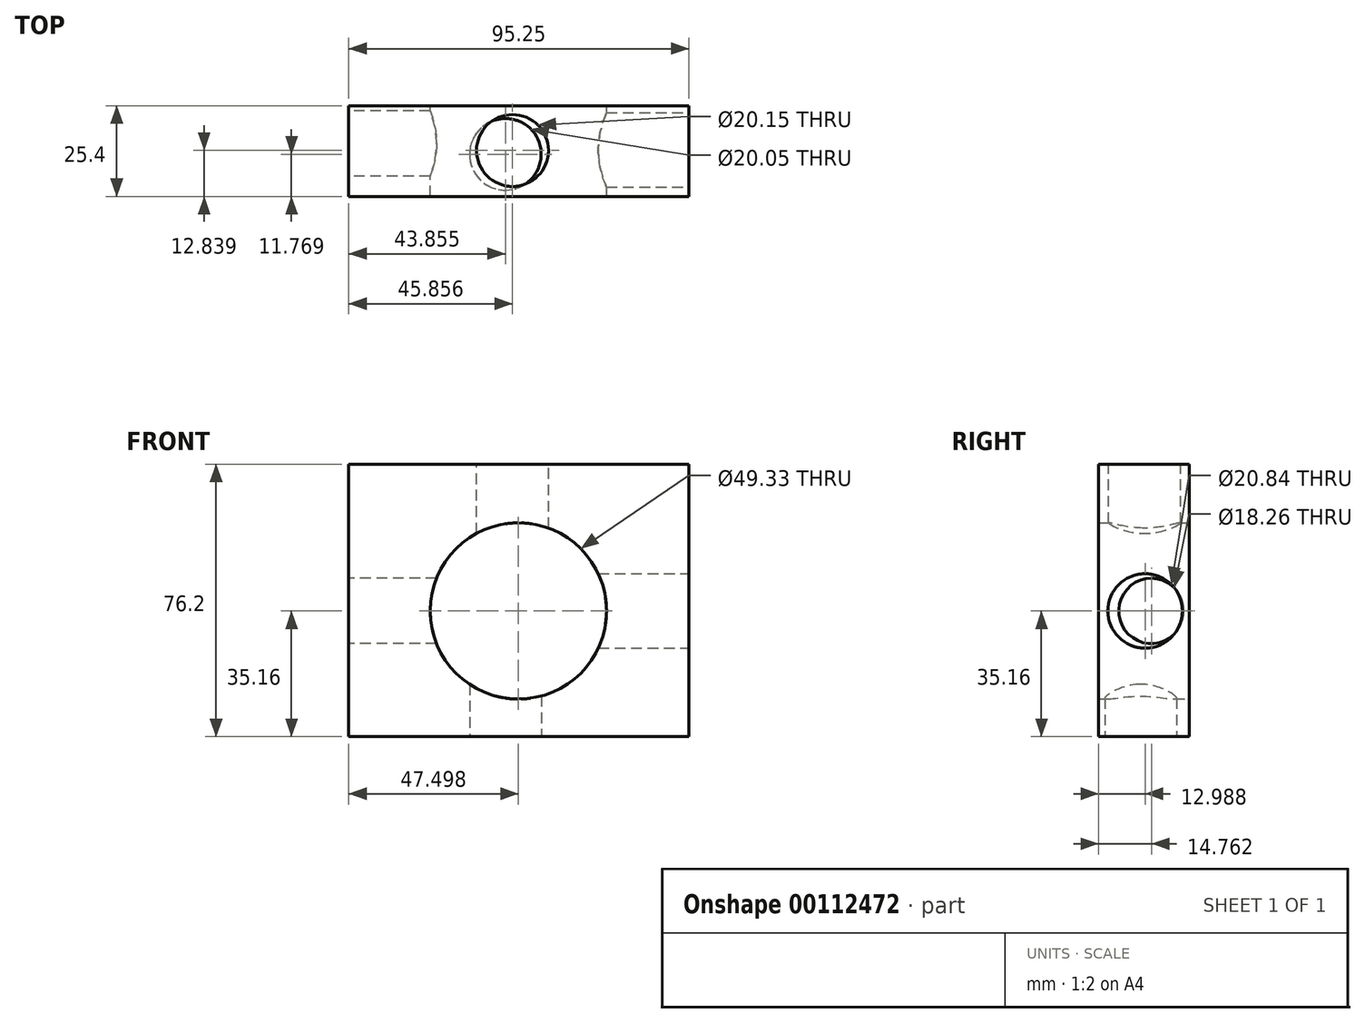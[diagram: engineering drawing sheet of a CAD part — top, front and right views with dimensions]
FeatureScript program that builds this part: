
annotation { "Feature Type Name" : "Feature", "Feature Type Description" : "" }
export const myFeature = defineFeature(function(context is Context, id is Id, definition is map)
    precondition{}
    {
        {
            var Q0;
            Q0=qCreatedBy(makeId("Front.planeOp"),FACE);
            var sketch = newSketch(context, id + "F0", { "sketchPlane" : qUnion([Q0])});
            skLineSegment(sketch, "E0", {"start": v(-95.25, 41.04) * mm, "end": v(0, 41.04) * mm});
            skLineSegment(sketch, "E1", {"start": v(0, 41.04) * mm, "end": v(0, -35.16) * mm});
            skLineSegment(sketch, "E2", {"start": v(0, -35.16) * mm, "end": v(-95.25, -35.16) * mm});
            skLineSegment(sketch, "E3", {"start": v(-95.25, -35.16) * mm, "end": v(-95.25, 41.04) * mm});
            skCircle(sketch, "E4", {"center": v(-47.75, 0) * mm, "radius": 24.67 * mm});
            skSolve(sketch);
        }
        {
            var Q0;
            Q0=makeQuery(id+"F0.imprint","IMPRINT",FACE,{"disambiguationData":[TD([[makeQuery(id+"F0.imprint","IMPRINT",EDGE,{"derivedFrom":sQuery(id+"F0.wireOp",EDGE,"E0")}),-1.0]])]});
            extrude(context, id + "F1", {"entities" : qUnion([Q0]), "depth" : 25.4 * mm});
        }
        {
            var Q0;
            Q0=makeQuery(id+"F1.opExtrude","SWEPT_FACE",FACE,{"disambiguationData":[OSD([sQuery(id+"F0.wireOp",EDGE,"E0")])]});
            var sketch = newSketch(context, id + "F2", { "sketchPlane" : qUnion([Q0])});
            skSolve(sketch);
        }
        {
            var Q0;
            {var subQ0=sQuery(id+"F0.wireOp",EDGE,"E0");Q0=makeQuery(id+"F2.imprint","IMPRINT",FACE,{"disambiguationData":[TD([[makeQuery(id+"F2.imprint","IMPRINT",EDGE,{"derivedFrom":makeQuery(id+"F1.opExtrude","CAP_EDGE",EDGE,{"disambiguationData":[OSD([subQ0])],"isStart":true})}),-1.0]])]});}
            var sketch = newSketch(context, id + "F3", { "sketchPlane" : qUnion([Q0])});
            skCircle(sketch, "E5", {"center": v(-49.4, -12.56) * mm, "radius": 10.07 * mm});
            skSolve(sketch);
        }
        {
            var Q0;
            Q0 = qSketchRegion(id + "F3", true);
            extrude(context, id + "F4", {"entities" : qUnion([Q0]), "operationType" : NewBodyOperationType.REMOVE, "oppositeDirection" : true, "depth" : 25.4 * mm});
        }
        {
            var Q0;
            Q0=makeQuery(id+"F1.opExtrude","SWEPT_FACE",FACE,{"disambiguationData":[OSD([sQuery(id+"F0.wireOp",EDGE,"E1")])]});
            var sketch = newSketch(context, id + "F5", { "sketchPlane" : qUnion([Q0])});
            skCircle(sketch, "E6", {"center": v(-12.41, 0) * mm, "radius": 10.42 * mm});
            skSolve(sketch);
        }
        {
            var Q0;
            Q0 = qSketchRegion(id + "F5", true);
            extrude(context, id + "F6", {"entities" : qUnion([Q0]), "operationType" : NewBodyOperationType.REMOVE, "oppositeDirection" : true, "depth" : 25.4 * mm});
        }
        {
            var Q0;
            Q0=makeQuery(id+"F1.opExtrude","SWEPT_FACE",FACE,{"disambiguationData":[OSD([sQuery(id+"F0.wireOp",EDGE,"E3")])]});
            var sketch = newSketch(context, id + "F7", { "sketchPlane" : qUnion([Q0])});
            skCircle(sketch, "E7", {"center": v(10.64, 0) * mm, "radius": 9.13 * mm});
            skSolve(sketch);
        }
        {
            var Q0;
            Q0 = qSketchRegion(id + "F7", true);
            extrude(context, id + "F8", {"entities" : qUnion([Q0]), "operationType" : NewBodyOperationType.REMOVE, "oppositeDirection" : true, "depth" : 25.4 * mm});
        }
        {
            var Q0;
            Q0=makeQuery(id+"F1.opExtrude","SWEPT_FACE",FACE,{"disambiguationData":[OSD([sQuery(id+"F0.wireOp",EDGE,"E2")])]});
            var sketch = newSketch(context, id + "F9", { "sketchPlane" : qUnion([Q0])});
            skSolve(sketch);
        }
        {
            var Q0;
            {var subQ0=sQuery(id+"F0.wireOp",EDGE,"E2");Q0=makeQuery(id+"F9.imprint","IMPRINT",FACE,{"disambiguationData":[TD([[makeQuery(id+"F9.imprint","IMPRINT",EDGE,{"derivedFrom":makeQuery(id+"F1.opExtrude","CAP_EDGE",EDGE,{"disambiguationData":[OSD([subQ0])],"isStart":true})}),-1.0]])]});}
            var sketch = newSketch(context, id + "F10", { "sketchPlane" : qUnion([Q0])});
            skCircle(sketch, "E8", {"center": v(-51.4, 13.63) * mm, "radius": 10.02 * mm});
            skSolve(sketch);
        }
        {
            var Q0;
            Q0 = qSketchRegion(id + "F10", true);
            extrude(context, id + "F11", {"entities" : qUnion([Q0]), "operationType" : NewBodyOperationType.REMOVE, "oppositeDirection" : true, "depth" : 25.4 * mm});
        }
    });
